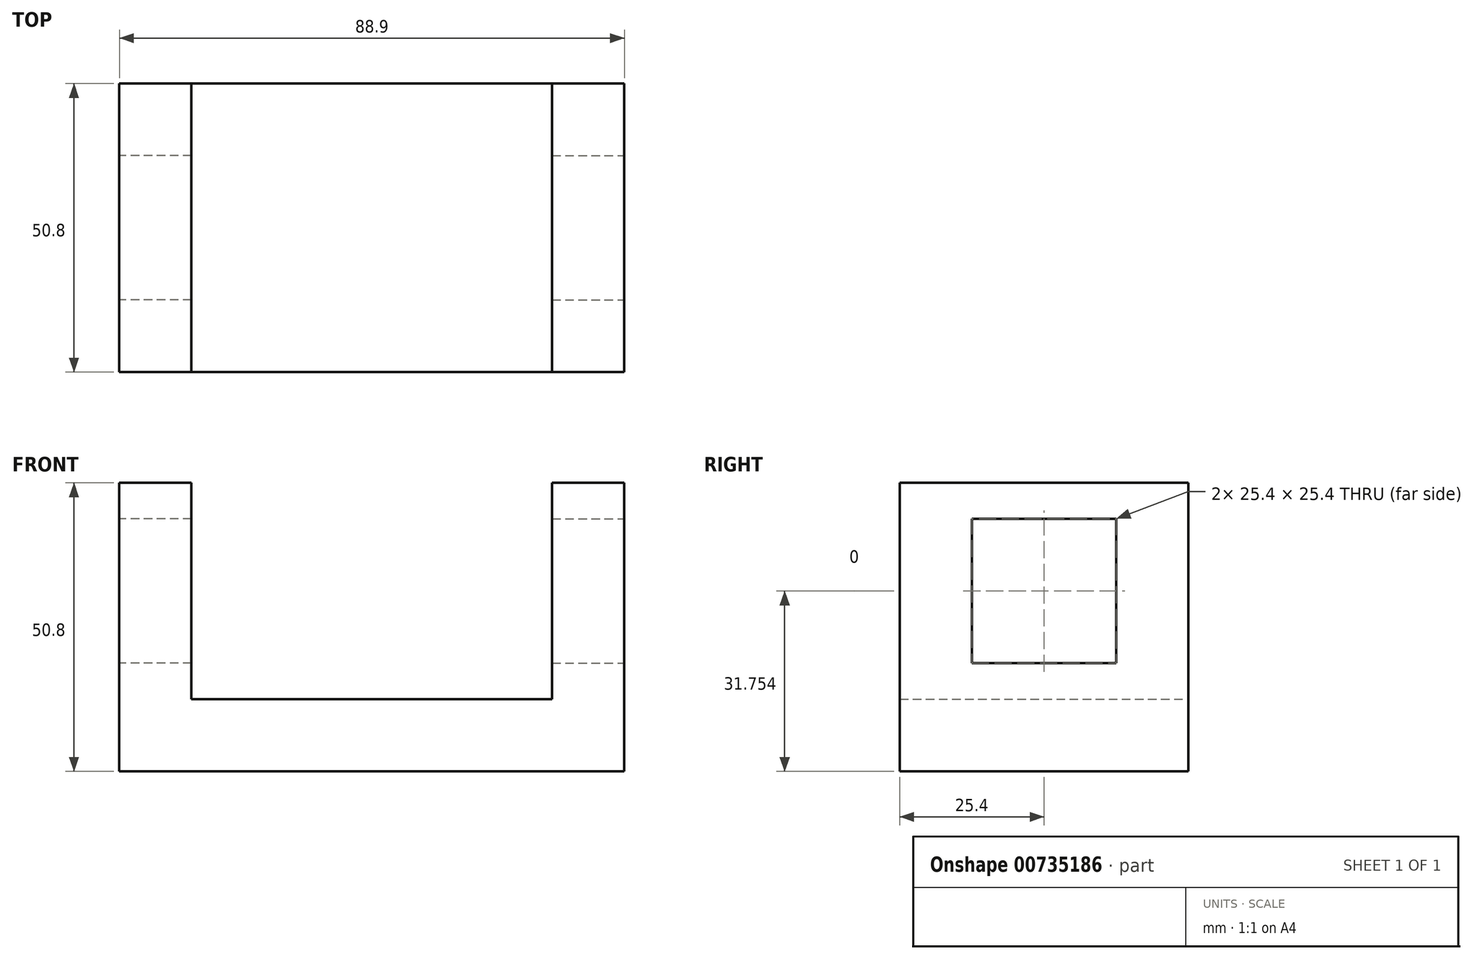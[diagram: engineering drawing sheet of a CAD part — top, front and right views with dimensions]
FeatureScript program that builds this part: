
annotation { "Feature Type Name" : "Feature", "Feature Type Description" : "" }
export const myFeature = defineFeature(function(context is Context, id is Id, definition is map)
    precondition{}
    {
        {
            var Q0;
            Q0=qCreatedBy(makeId("Front.planeOp"),FACE);
            var sketch = newSketch(context, id + "F0", { "sketchPlane" : qUnion([Q0])});
            skLineSegment(sketch, "E0", {"start": v(-65.47, 24.63) * mm, "end": v(-65.47, -26.17) * mm});
            skLineSegment(sketch, "E1", {"start": v(-65.47, -26.17) * mm, "end": v(23.43, -26.17) * mm});
            skLineSegment(sketch, "E2", {"start": v(23.43, -26.17) * mm, "end": v(23.43, 24.63) * mm});
            skLineSegment(sketch, "E3", {"start": v(23.43, 24.63) * mm, "end": v(10.73, 24.63) * mm});
            skLineSegment(sketch, "E4", {"start": v(10.73, 24.63) * mm, "end": v(10.73, -13.47) * mm});
            skLineSegment(sketch, "E5", {"start": v(-52.77, 24.63) * mm, "end": v(-52.77, -13.47) * mm});
            skLineSegment(sketch, "E6", {"start": v(-52.77, -13.47) * mm, "end": v(10.73, -13.47) * mm});
            skLineSegment(sketch, "E7", {"start": v(-65.47, 24.63) * mm, "end": v(-52.77, 24.63) * mm});
            skSolve(sketch);
        }
        {
            var Q0;
            Q0=qCreatedBy(makeId("Right.planeOp"),FACE);
            var sketch = newSketch(context, id + "F1", { "sketchPlane" : qUnion([Q0])});
            skSolve(sketch);
        }
        {
            var Q0;
            Q0 = qSketchRegion(id + "F1", true);
            var Q1;
            Q1=makeQuery(id+"F0.imprint","IMPRINT",FACE,{"disambiguationData":[TD([[makeQuery(id+"F0.imprint","IMPRINT",EDGE,{"derivedFrom":sQuery(id+"F0.wireOp",EDGE,"E0")}),1.0]])]});
            extrude(context, id + "F2", {"entities" : qUnion([Q0, Q1]), "depth" : 50.8 * mm, "offsetDistance" : 25.4 * mm});
        }
        {
            var Q0;
            Q0=makeQuery(id+"F2.opExtrude","SWEPT_FACE",FACE,{"disambiguationData":[OSD([sQuery(id+"F0.wireOp",EDGE,"E2")])]});
            var sketch = newSketch(context, id + "F3", { "sketchPlane" : qUnion([Q0])});
            skLineSegment(sketch, "E8", {"start": v(-38.1, 18.28) * mm, "end": v(-12.7, 18.28) * mm});
            skLineSegment(sketch, "E9", {"start": v(-12.7, 18.28) * mm, "end": v(-12.7, -7.12) * mm});
            skLineSegment(sketch, "E10", {"start": v(-12.7, -7.12) * mm, "end": v(-38.1, -7.12) * mm});
            skLineSegment(sketch, "E11", {"start": v(-38.1, -7.12) * mm, "end": v(-38.1, 18.28) * mm});
            skLineSegment(sketch, "E12", {"start": v(-38.1, -7.12) * mm, "end": v(-50.8, -7.12) * mm});
            skLineSegment(sketch, "E13", {"start": v(-50.8, -7.12) * mm, "end": v(-50.8, -26.17) * mm});
            skPoint(sketch, "E14.end.orphan", {"position": v(0, -0.77) * mm});
            skPoint(sketch, "E14.start.orphan", {"position": v(-12.7, 5.58) * mm});
            skSolve(sketch);
        }
        {
            var Q0;
            {var subQ3=sQuery(id+"F3.wireOp",EDGE,"E8");Q0=makeQuery(id+"F3.imprint","IMPRINT",FACE,{"disambiguationData":[TD([[makeQuery(id+"F3.imprint","IMPRINT",EDGE,{"derivedFrom":subQ3}),-1.0]])]});}
            extrude(context, id + "F4", {"entities" : qUnion([Q0]), "operationType" : NewBodyOperationType.REMOVE, "oppositeDirection" : true, "depth" : 12.7 * mm, "offsetDistance" : 25.4 * mm});
        }
        {
            var Q0;
            Q0=makeQuery(id+"F2.opExtrude","SWEPT_FACE",FACE,{"disambiguationData":[OSD([sQuery(id+"F0.wireOp",EDGE,"E0")])]});
            var sketch = newSketch(context, id + "F5", { "sketchPlane" : qUnion([Q0])});
            skLineSegment(sketch, "E15", {"start": v(12.7, 18.28) * mm, "end": v(38.1, 18.28) * mm});
            skLineSegment(sketch, "E16", {"start": v(38.1, 18.28) * mm, "end": v(38.1, -7.12) * mm});
            skLineSegment(sketch, "E17", {"start": v(38.1, -7.12) * mm, "end": v(12.7, -7.12) * mm});
            skLineSegment(sketch, "E18", {"start": v(12.7, -7.12) * mm, "end": v(12.7, 18.28) * mm});
            skLineSegment(sketch, "E19", {"start": v(12.7, 5.58) * mm, "end": v(0, 5.58) * mm});
            skPoint(sketch, "E19.endSnap0", {"position": v(12.7, 5.58) * mm});
            skLineSegment(sketch, "E20", {"start": v(25.4, -7.12) * mm, "end": v(25.4, -26.17) * mm});
            skSolve(sketch);
        }
        {
            var Q0;
            {var subQ5=sQuery(id+"F5.wireOp",EDGE,"E15");Q0=makeQuery(id+"F5.imprint","IMPRINT",FACE,{"disambiguationData":[TD([[makeQuery(id+"F5.imprint","IMPRINT",EDGE,{"derivedFrom":subQ5}),-1.0]])]});}
            extrude(context, id + "F6", {"entities" : qUnion([Q0]), "operationType" : NewBodyOperationType.REMOVE, "oppositeDirection" : true, "depth" : 12.7 * mm, "offsetDistance" : 25.4 * mm});
        }
    });
